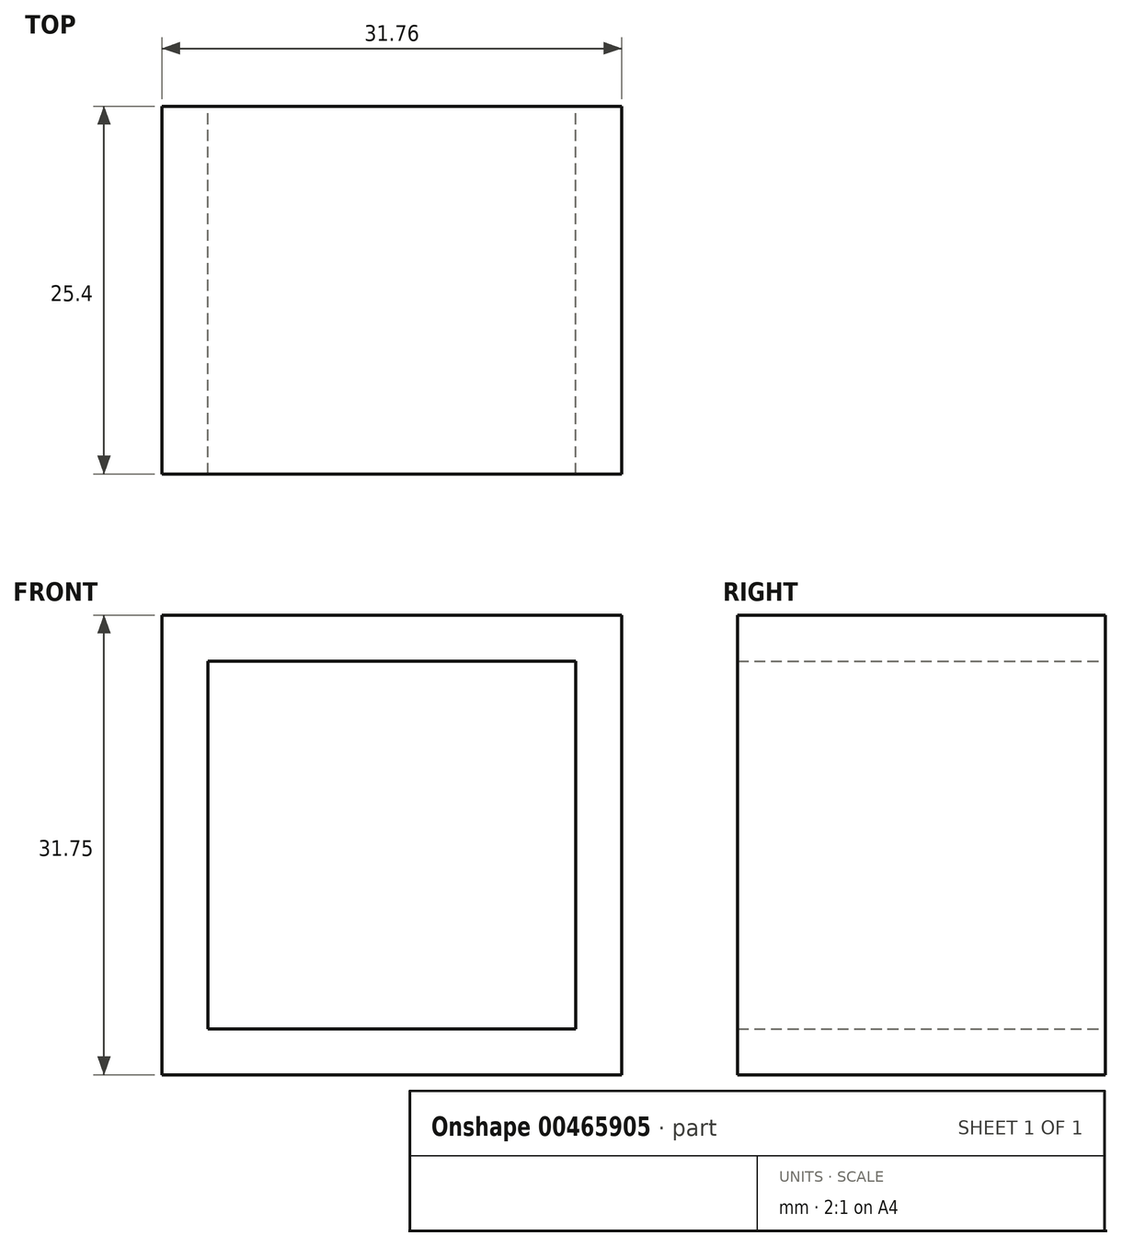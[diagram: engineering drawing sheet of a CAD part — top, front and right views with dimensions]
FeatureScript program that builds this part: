
annotation { "Feature Type Name" : "Feature", "Feature Type Description" : "" }
export const myFeature = defineFeature(function(context is Context, id is Id, definition is map)
    precondition{}
    {
        {
            var Q0;
            Q0=qCreatedBy(makeId("Front.planeOp"),FACE);
            var sketch = newSketch(context, id + "F0", { "sketchPlane" : qUnion([Q0])});
            skLineSegment(sketch, "E0.bottom", {"start": v(-15.88, 13.18) * mm, "end": v(15.88, 13.18) * mm});
            skLineSegment(sketch, "E0.top", {"start": v(-15.88, -18.57) * mm, "end": v(15.88, -18.57) * mm});
            skLineSegment(sketch, "E0.left", {"start": v(-15.88, 13.18) * mm, "end": v(-15.88, -18.57) * mm});
            skLineSegment(sketch, "E0.right", {"start": v(15.88, 13.18) * mm, "end": v(15.87, -18.57) * mm});
            skPoint(sketch, "E0.middle", {"position": v(0, -2.7) * mm});
            skLineSegment(sketch, "E1.bottom", {"start": v(-12.7, 10) * mm, "end": v(12.7, 10) * mm});
            skLineSegment(sketch, "E1.top", {"start": v(-12.7, -15.4) * mm, "end": v(12.7, -15.4) * mm});
            skLineSegment(sketch, "E1.left", {"start": v(-12.7, 10) * mm, "end": v(-12.7, -15.4) * mm});
            skLineSegment(sketch, "E1.right", {"start": v(12.7, 10) * mm, "end": v(12.7, -15.4) * mm});
            skSolve(sketch);
        }
        {
            var Q0;
            Q0=makeQuery(id+"F0.imprint","IMPRINT",FACE,{"disambiguationData":[TD([[makeQuery(id+"F0.imprint","IMPRINT",EDGE,{"derivedFrom":sQuery(id+"F0.wireOp",EDGE,"E0.bottom")}),-1.0]])]});
            extrude(context, id + "F1", {"entities" : qUnion([Q0]), "depth" : 25.4 * mm});
        }
    });
